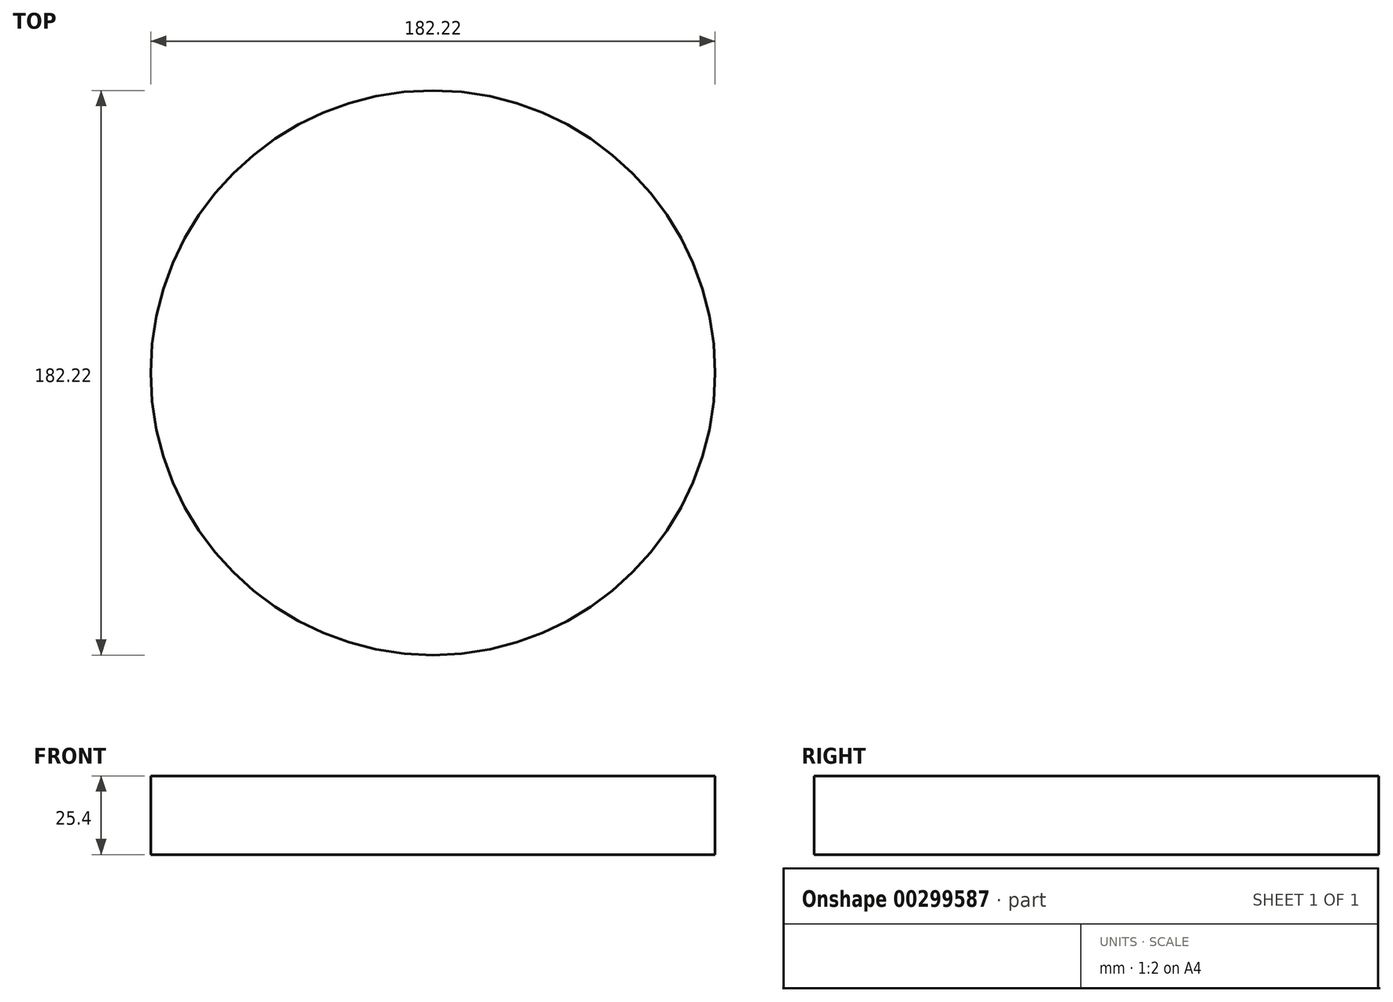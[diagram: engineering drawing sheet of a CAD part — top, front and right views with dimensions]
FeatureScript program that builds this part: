
annotation { "Feature Type Name" : "Feature", "Feature Type Description" : "" }
export const myFeature = defineFeature(function(context is Context, id is Id, definition is map)
    precondition{}
    {
        {
            var Q0;
            Q0=qCreatedBy(makeId("Top.planeOp"),FACE);
            var sketch = newSketch(context, id + "F0", { "sketchPlane" : qUnion([Q0])});
            skCircle(sketch, "E0", {"center": v(0, 0) * mm, "radius": 91.1 * mm});
            skSolve(sketch);
        }
        {
            var Q0;
            Q0=makeQuery(id+"F0.imprint","IMPRINT",FACE,{"disambiguationData":[TD([[makeQuery(id+"F0.imprint","IMPRINT",EDGE,{"derivedFrom":sQuery(id+"F0.wireOp",EDGE,"E0")}),1.0]])]});
            extrude(context, id + "F1", {"entities" : qUnion([Q0]), "oppositeDirection" : true, "depth" : 25.4 * mm});
        }
    });
